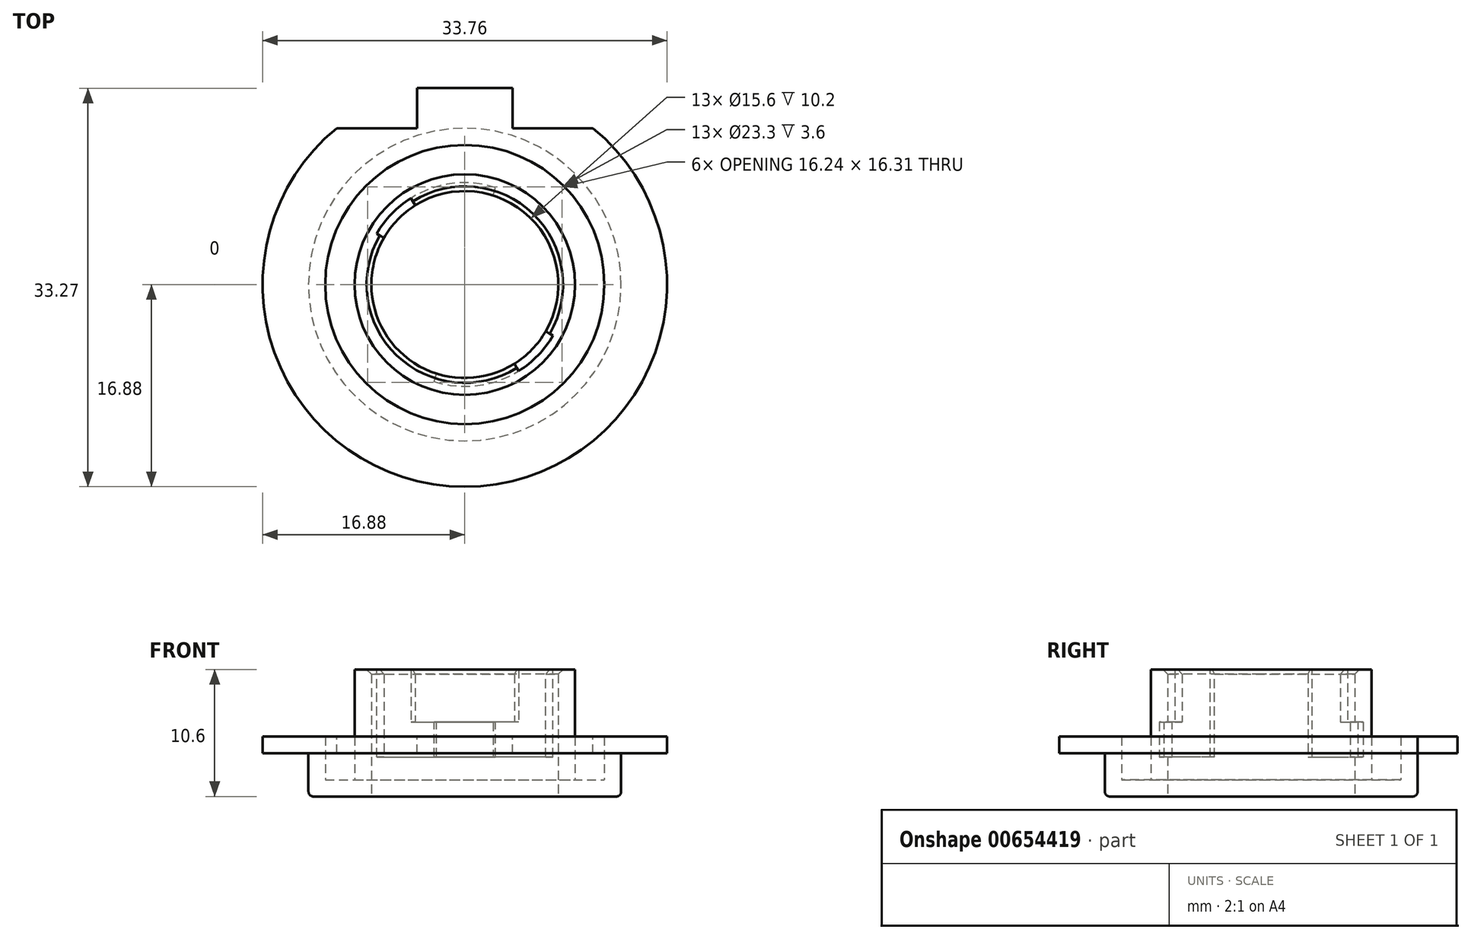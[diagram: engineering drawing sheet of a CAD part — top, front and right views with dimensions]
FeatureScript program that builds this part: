
annotation { "Feature Type Name" : "Feature", "Feature Type Description" : "" }
export const myFeature = defineFeature(function(context is Context, id is Id, definition is map)
    precondition{}
    {
        {
            var Q0;
            Q0=qCreatedBy(makeId("Front.planeOp"),FACE);
            var sketch = newSketch(context, id + "F0", { "sketchPlane" : qUnion([Q0])});
            skLineSegment(sketch, "E0", {"start": v(0, 0) * mm, "end": v(0, 105.8) * mm, "construction": true});
            skLineSegment(sketch, "E1", {"start": v(-7.8, 15.02) * mm, "end": v(-13.05, 15.02) * mm});
            skLineSegment(sketch, "E2", {"start": v(-13.05, 15.02) * mm, "end": v(-13.05, 18.62) * mm});
            skLineSegment(sketch, "E3", {"start": v(-13.05, 18.62) * mm, "end": v(-16.88, 18.62) * mm});
            skLineSegment(sketch, "E4", {"start": v(-7.8, 25.62) * mm, "end": v(-7.8, 15.02) * mm});
            skLineSegment(sketch, "E5.0", {"start": v(-11.65, 20.02) * mm, "end": v(-16.88, 20.02) * mm});
            skLineSegment(sketch, "E5.1", {"start": v(-11.65, 16.42) * mm, "end": v(-11.65, 20.02) * mm});
            skLineSegment(sketch, "E5.2", {"start": v(-9.2, 16.42) * mm, "end": v(-11.65, 16.42) * mm});
            skLineSegment(sketch, "E5.3", {"start": v(-9.2, 25.62) * mm, "end": v(-9.2, 16.42) * mm});
            skLineSegment(sketch, "E6", {"start": v(-9.2, 25.62) * mm, "end": v(-7.8, 25.62) * mm});
            skLineSegment(sketch, "E7", {"start": v(-16.88, 20.02) * mm, "end": v(-16.88, 18.62) * mm});
            skSolve(sketch);
        }
        {
            var Q0;
            Q0=makeQuery(id+"F0.imprint","IMPRINT",FACE,{"disambiguationData":[TD([[makeQuery(id+"F0.imprint","IMPRINT",EDGE,{"derivedFrom":sQuery(id+"F0.wireOp",EDGE,"E1")}),-1.0]])]});
            var Q1;
            Q1=sQuery(id+"F0.wireOp",EDGE,"E0");
            revolve(context, id + "F1", {"entities" : qUnion([Q0]), "axis" : qUnion([Q1]), "revolveType" : RevolveType.FULL});
        }
        {
            var Q0;
            Q0=makeQuery(id+"F1.opRevolve","SWEPT_FACE",FACE,{"disambiguationData":[OSD([sQuery(id+"F0.wireOp",EDGE,"E5.0")])]});
            var sketch = newSketch(context, id + "F2", { "sketchPlane" : qUnion([Q0])});
            skLineSegment(sketch, "E8", {"start": v(0, 19.6) * mm, "end": v(0, -24.8) * mm, "construction": true});
            skLineSegment(sketch, "E9", {"start": v(-16.15, 13.05) * mm, "end": v(16.92, 13.05) * mm, "construction": true});
            skLineSegment(sketch, "E10", {"start": v(-4, 16.4) * mm, "end": v(-4, 13.05) * mm});
            skLineSegment(sketch, "E11", {"start": v(-4, 13.05) * mm, "end": v(-10.7, 13.05) * mm});
            skLineSegment(sketch, "E12", {"start": v(-4, 16.4) * mm, "end": v(4, 16.4) * mm});
            skLineSegment(sketch, "E13", {"start": v(4, 16.4) * mm, "end": v(4, 13.05) * mm});
            skLineSegment(sketch, "E14", {"start": v(4, 13.05) * mm, "end": v(10.7, 13.05) * mm});
            skCircle(sketch, "E15.0", {"center": v(0, 0) * mm, "radius": 13.05 * mm});
            skSolve(sketch);
        }
        {
            var Q0;
            {var subQ0=sQuery(id+"F2.wireOp",EDGE,"E10");Q0=makeQuery(id+"F2.imprint","IMPRINT",FACE,{"disambiguationData":[TD([[makeQuery(id+"F2.imprint","IMPRINT",EDGE,{"derivedFrom":subQ0}),-1.0]])]});}
            var Q1;
            {var subQ0=sQuery(id+"F2.wireOp",EDGE,"E13");Q1=makeQuery(id+"F2.imprint","IMPRINT",FACE,{"disambiguationData":[TD([[makeQuery(id+"F2.imprint","IMPRINT",EDGE,{"derivedFrom":subQ0}),1.0]])]});}
            var Q2;
            {var subQ0=sQuery(id+"F2.wireOp",EDGE,"E12");Q2=makeQuery(id+"F2.imprint","IMPRINT",FACE,{"disambiguationData":[TD([[makeQuery(id+"F2.imprint","IMPRINT",EDGE,{"derivedFrom":subQ0}),1.0]])]});}
            extrude(context, id + "F3", {"entities" : qUnion([Q0, Q1, Q2]), "operationType" : NewBodyOperationType.REMOVE, "endBound" : BoundingType.THROUGH_ALL, "oppositeDirection" : true, "depth" : 25 * mm, "offsetDistance" : 25 * mm});
        }
        {
            var Q0;
            Q0=qCreatedBy(makeId("Right.planeOp"),FACE);
            var sketch = newSketch(context, id + "F4", { "sketchPlane" : qUnion([Q0])});
            skLineSegment(sketch, "E16", {"start": v(7.8, 18.32) * mm, "end": v(8.5, 18.32) * mm});
            skLineSegment(sketch, "E17", {"start": v(8.5, 18.32) * mm, "end": v(8.5, 21.22) * mm});
            skLineSegment(sketch, "E18", {"start": v(8.5, 21.22) * mm, "end": v(7.8, 21.22) * mm});
            skLineSegment(sketch, "E19", {"start": v(7.8, 25.62) * mm, "end": v(7.8, 15.02) * mm});
            skLineSegment(sketch, "E20", {"start": v(-7.8, 15.02) * mm, "end": v(-7.8, 25.62) * mm});
            skLineSegment(sketch, "E21", {"start": v(9.2, 25.62) * mm, "end": v(9.2, 16.42) * mm});
            skLineSegment(sketch, "E22", {"start": v(-9.2, 16.42) * mm, "end": v(-9.2, 25.62) * mm});
            skLineSegment(sketch, "E23.MirrorCS", {"start": v(-7.8, 18.32) * mm, "end": v(-8.5, 18.32) * mm});
            skLineSegment(sketch, "E24.MirrorCS", {"start": v(-8.5, 18.32) * mm, "end": v(-8.5, 21.22) * mm});
            skLineSegment(sketch, "E25.MirrorCS", {"start": v(-8.5, 21.22) * mm, "end": v(-7.8, 21.22) * mm});
            skSolve(sketch);
        }
        {
            var Q0;
            Q0 = qSketchRegion(id + "F4", true);
            var Q1;
            Q1=makeQuery(id+"F1.opRevolve","SWEPT_EDGE",EDGE,{"disambiguationData":[OSD([sQuery(id+"F0.wireOp",EDGE,"E4"),sQuery(id+"F0.wireOp",EDGE,"E6")])]});
            revolve(context, id + "F5", {"operationType" : NewBodyOperationType.REMOVE, "entities" : qUnion([Q0]), "axis" : qUnion([Q1]), "revolveType" : RevolveType.TWO_DIRECTIONS, "oppositeDirection" : true, "angle" : 60 * degree, "angleBack" : 342.41 * degree});
        }
        {
            var Q0;
            Q0=qCreatedBy(makeId("Right.planeOp"),FACE);
            var sketch = newSketch(context, id + "F6", { "sketchPlane" : qUnion([Q0])});
            skLineSegment(sketch, "E26", {"start": v(-7.8, 21.22) * mm, "end": v(-7.8, 25.62) * mm, "construction": true});
            skLineSegment(sketch, "E27", {"start": v(7.8, 25.62) * mm, "end": v(7.8, 21.22) * mm, "construction": true});
            skLineSegment(sketch, "E28", {"start": v(7.8, 18.32) * mm, "end": v(7.8, 15.02) * mm, "construction": true});
            skLineSegment(sketch, "E29", {"start": v(-7.8, 15.02) * mm, "end": v(-7.8, 18.32) * mm, "construction": true});
            skLineSegment(sketch, "E30.0", {"start": v(13.05, 15.02) * mm, "end": v(-13.05, 15.02) * mm, "construction": true});
            skLineSegment(sketch, "E31", {"start": v(8.5, 18.32) * mm, "end": v(8.5, 21.22) * mm, "construction": true});
            skLineSegment(sketch, "E32", {"start": v(7.8, 18.32) * mm, "end": v(8.5, 18.32) * mm, "construction": true});
            skLineSegment(sketch, "E33", {"start": v(8.5, 21.22) * mm, "end": v(7.8, 21.22) * mm, "construction": true});
            skLineSegment(sketch, "E34", {"start": v(7.8, 18.32) * mm, "end": v(8.5, 18.32) * mm});
            skLineSegment(sketch, "E35", {"start": v(8.5, 25.62) * mm, "end": v(7.8, 25.62) * mm});
            skLineSegment(sketch, "E36", {"start": v(8.5, 25.62) * mm, "end": v(8.5, 18.32) * mm});
            skLineSegment(sketch, "E37", {"start": v(7.8, 25.62) * mm, "end": v(7.8, 18.32) * mm});
            skLineSegment(sketch, "E38.MirrorCS", {"start": v(-7.8, 18.32) * mm, "end": v(-8.5, 18.32) * mm, "construction": true});
            skLineSegment(sketch, "E39.MirrorCS", {"start": v(-7.8, 18.32) * mm, "end": v(-8.5, 18.32) * mm});
            skLineSegment(sketch, "E40.MirrorCS", {"start": v(-8.5, 25.62) * mm, "end": v(-7.8, 25.62) * mm});
            skLineSegment(sketch, "E41.MirrorCS", {"start": v(-7.8, 25.62) * mm, "end": v(-7.8, 21.22) * mm, "construction": true});
            skLineSegment(sketch, "E42.MirrorCS", {"start": v(-8.5, 18.32) * mm, "end": v(-8.5, 21.22) * mm, "construction": true});
            skLineSegment(sketch, "E43.MirrorCS", {"start": v(-8.5, 25.62) * mm, "end": v(-8.5, 18.32) * mm});
            skLineSegment(sketch, "E44.MirrorCS", {"start": v(-7.8, 25.62) * mm, "end": v(-7.8, 18.32) * mm});
            skSolve(sketch);
        }
        {
            var Q0;
            Q0 = qSketchRegion(id + "F6", true);
            var Q1;
            Q1=makeQuery(id+"F1.opRevolve","SWEPT_FACE",FACE,{"disambiguationData":[OSD([sQuery(id+"F0.wireOp",EDGE,"E4")])]});
            revolve(context, id + "F7", {"operationType" : NewBodyOperationType.REMOVE, "entities" : qUnion([Q0]), "axis" : qUnion([Q1]), "revolveType" : RevolveType.TWO_DIRECTIONS, "oppositeDirection" : true, "angle" : 328 * degree, "angleBack" : 300 * degree});
        }
        {
            var Q0;
            {var subQ0=sQuery(id+"F0.wireOp",EDGE,"E4");var subQ1=sQuery(id+"F0.wireOp",EDGE,"E6");Q0=makeQuery(id+"F7.boolean.opBoolean","SPLIT",EDGE,{"disambiguationData":[TD([makeQuery(id+"F5.boolean.opBoolean","COPY",FACE,{"derivedFrom":makeQuery(id+"F5.opRevolve","CAP_FACE",FACE,{"disambiguationData":[OSD([sQuery(id+"F4.wireOp",EDGE,"E20"),sQuery(id+"F4.wireOp",EDGE,"E23.MirrorCS"),sQuery(id+"F4.wireOp",EDGE,"E24.MirrorCS"),sQuery(id+"F4.wireOp",EDGE,"E25.MirrorCS")])],"isStart":false})})])],"derivedFrom":makeQuery(id+"F1.opRevolve","SWEPT_EDGE",EDGE,{"disambiguationData":[OSD([subQ0,subQ1])]})});}
            var Q1;
            {var subQ0=sQuery(id+"F0.wireOp",EDGE,"E6");var subQ1=sQuery(id+"F0.wireOp",EDGE,"E4");Q1=makeQuery(id+"F7.boolean.opBoolean","SPLIT",EDGE,{"disambiguationData":[TD([makeQuery(id+"F5.boolean.opBoolean","COPY",FACE,{"derivedFrom":makeQuery(id+"F5.opRevolve","CAP_FACE",FACE,{"disambiguationData":[OSD([sQuery(id+"F4.wireOp",EDGE,"E16"),sQuery(id+"F4.wireOp",EDGE,"E17"),sQuery(id+"F4.wireOp",EDGE,"E18"),sQuery(id+"F4.wireOp",EDGE,"E19")]),OD(0.0)],"isStart":false})})])],"derivedFrom":makeQuery(id+"F1.opRevolve","SWEPT_EDGE",EDGE,{"disambiguationData":[OSD([subQ1,subQ0])]})});}
            chamfer(context, id + "F8", {"entities" : qUnion([Q0, Q1]), "width" : 0.4 * mm, "tangentPropagation" : true});
        }
        {
            var Q0;
            Q0=makeQuery(id+"F1.opRevolve","SWEPT_EDGE",EDGE,{"disambiguationData":[OSD([sQuery(id+"F0.wireOp",EDGE,"E1"),sQuery(id+"F0.wireOp",EDGE,"E2")])]});
            fillet(context, id + "F9", {"entities" : qUnion([Q0]), "radius" : 0.4 * mm, "tangentPropagation" : true, "allowEdgeOverflow" : false});
        }
    });
